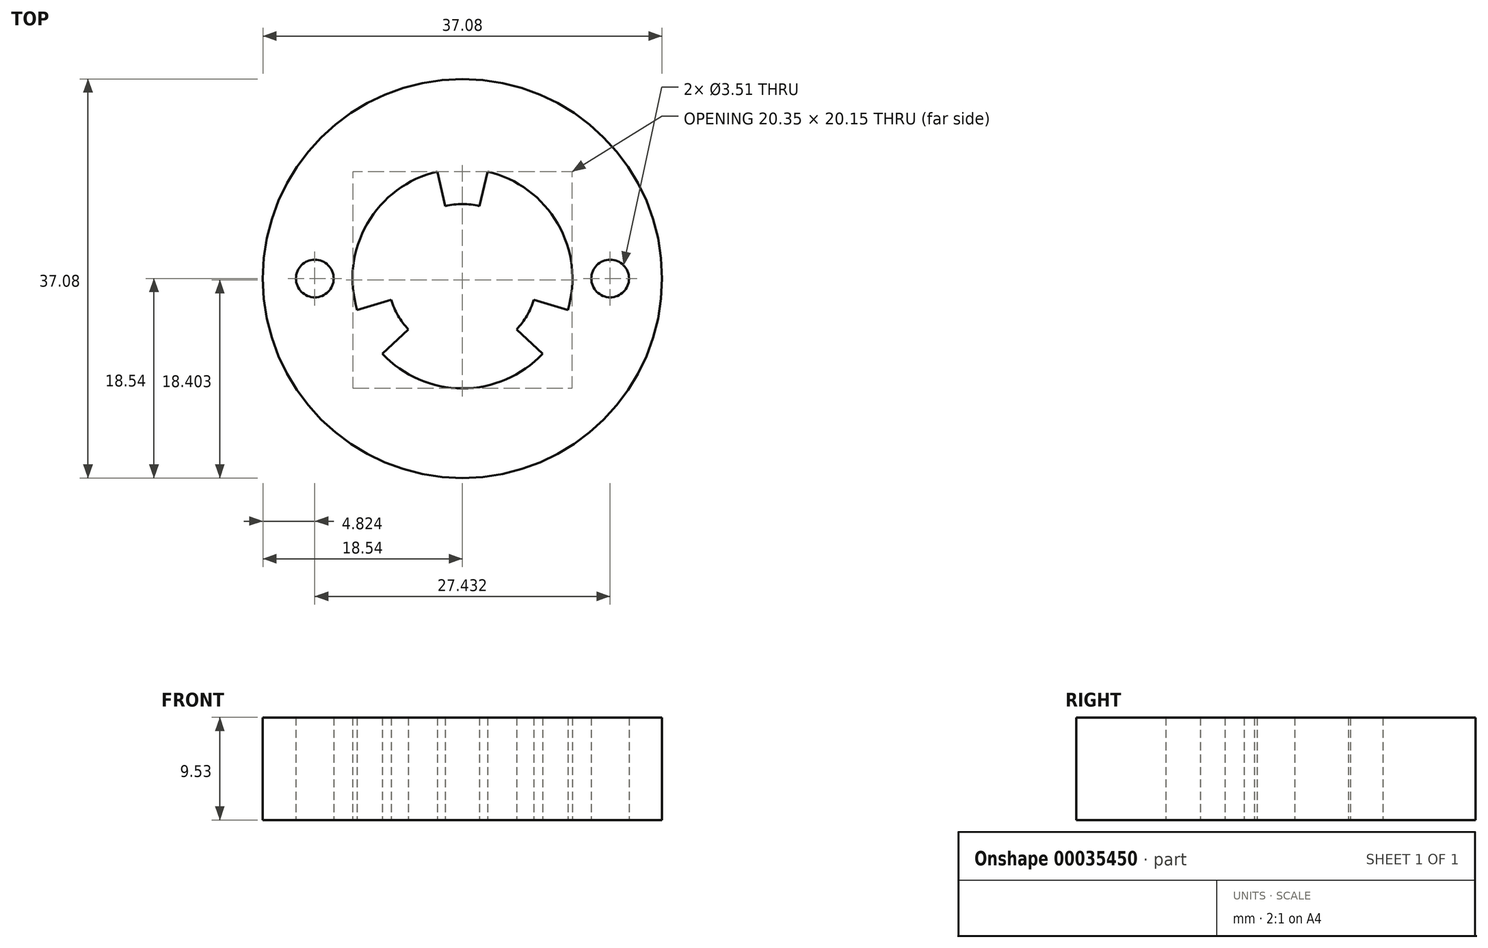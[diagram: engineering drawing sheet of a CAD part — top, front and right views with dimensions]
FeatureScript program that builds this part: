
annotation { "Feature Type Name" : "Feature", "Feature Type Description" : "" }
export const myFeature = defineFeature(function(context is Context, id is Id, definition is map)
    precondition{}
    {
        {
            var Q0;
            Q0=qCreatedBy(makeId("Top.planeOp"),FACE);
            var sketch = newSketch(context, id + "F0", { "sketchPlane" : qUnion([Q0])});
            skCircle(sketch, "E0", {"center": v(0, 0) * mm, "radius": 18.54 * mm});
            skLineSegment(sketch, "E1", {"start": v(-18.54, 0) * mm, "end": v(18.54, 0) * mm, "construction": true});
            skLineSegment(sketch, "E2", {"start": v(0, 18.54) * mm, "end": v(0, -18.54) * mm, "construction": true});
            skCircle(sketch, "E3", {"center": v(0, 0) * mm, "radius": 13.72 * mm, "construction": true});
            skCircle(sketch, "E4", {"center": v(-13.72, 0) * mm, "radius": 1.75 * mm});
            skCircle(sketch, "E5.MirrorC", {"center": v(13.72, 0) * mm, "radius": 1.75 * mm});
            skArc(sketch, "E6", {"start": v(-6.62, -1.99) * mm, "mid": v(-5.99, -3.46) * mm, "end": v(-5.03, -4.74) * mm});
            skArc(sketch, "E7.0", {"start": v(-7.44, -7) * mm, "mid": v(0, -10.21) * mm, "end": v(7.44, -7) * mm});
            skCircle(sketch, "E8", {"center": v(0, 6.91) * mm, "radius": 1.59 * mm, "construction": true});
            skLineSegment(sketch, "E9", {"start": v(-1.55, 6.55) * mm, "end": v(-2.35, 9.94) * mm});
            skLineSegment(sketch, "E10.MirrorCS", {"start": v(1.55, 6.55) * mm, "end": v(2.35, 9.94) * mm});
            skLineSegment(sketch, "E11.1.0", {"start": v(-6.44, -1.94) * mm, "end": v(-9.78, -2.94) * mm});
            skCircle(sketch, "E11.1.1", {"center": v(-5.99, -3.46) * mm, "radius": 1.59 * mm, "construction": true});
            skLineSegment(sketch, "E11.1.2", {"start": v(-4.9, -4.61) * mm, "end": v(-7.44, -7) * mm});
            skLineSegment(sketch, "E11.2.0", {"start": v(4.9, -4.61) * mm, "end": v(7.44, -7) * mm});
            skCircle(sketch, "E11.2.1", {"center": v(5.99, -3.46) * mm, "radius": 1.59 * mm, "construction": true});
            skLineSegment(sketch, "E11.2.2", {"start": v(6.44, -1.94) * mm, "end": v(9.78, -2.94) * mm});
            skArc(sketch, "E12.trimOffspring", {"start": v(5.03, -4.74) * mm, "mid": v(5.99, -3.46) * mm, "end": v(6.62, -1.99) * mm});
            skArc(sketch, "E13.trimOffspring", {"start": v(1.59, 6.73) * mm, "mid": v(0, 6.91) * mm, "end": v(-1.59, 6.73) * mm});
            skArc(sketch, "E14.trimOffspring", {"start": v(9.78, -2.94) * mm, "mid": v(8.84, 5.1) * mm, "end": v(2.35, 9.94) * mm});
            skArc(sketch, "E15.trimOffspring", {"start": v(-2.35, 9.94) * mm, "mid": v(-8.84, 5.1) * mm, "end": v(-9.78, -2.94) * mm});
            skSolve(sketch);
        }
        {
            var Q0;
            Q0=makeQuery(id+"F0.imprint","IMPRINT",FACE,{"disambiguationData":[TD([[makeQuery(id+"F0.imprint","IMPRINT",EDGE,{"derivedFrom":sQuery(id+"F0.wireOp",EDGE,"E0")}),1.0]])]});
            extrude(context, id + "F1", {"entities" : qUnion([Q0]), "depth" : 9.52 * mm});
        }
    });
